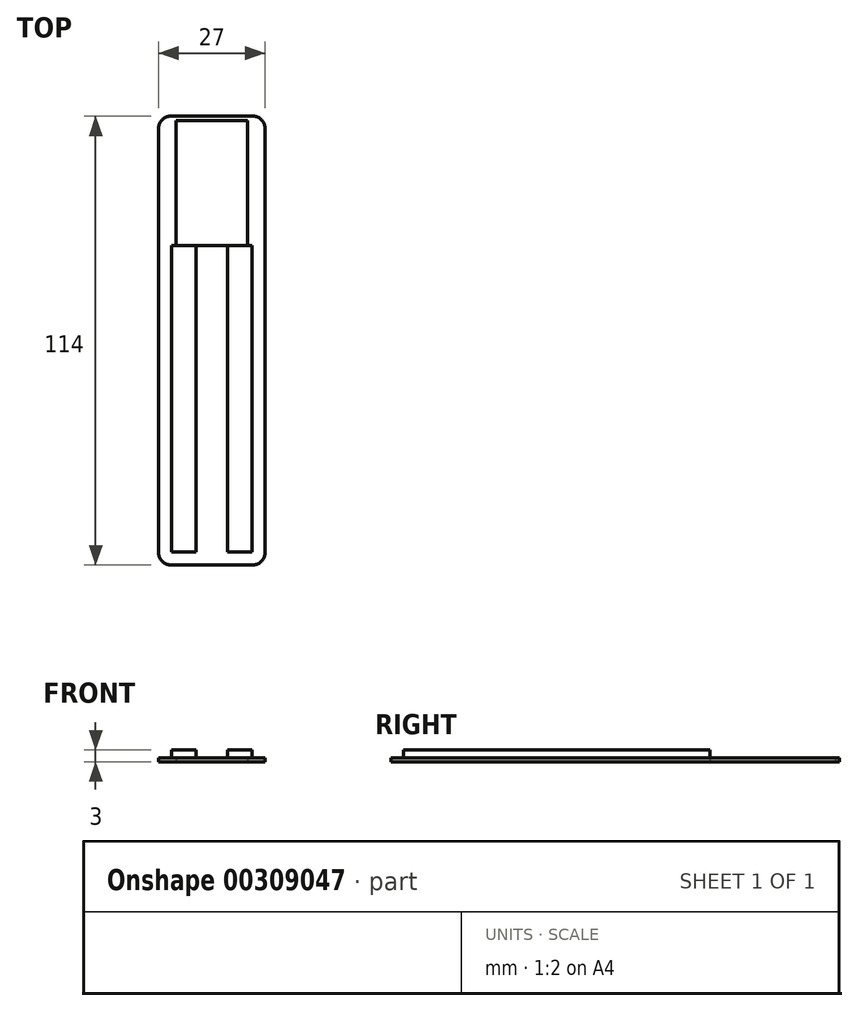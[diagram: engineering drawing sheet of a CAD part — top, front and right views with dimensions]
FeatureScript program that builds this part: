
annotation { "Feature Type Name" : "Feature", "Feature Type Description" : "" }
export const myFeature = defineFeature(function(context is Context, id is Id, definition is map)
    precondition{}
    {
        {
            var Q0;
            Q0=qCreatedBy(makeId("Top.planeOp"),FACE);
            var sketch = newSketch(context, id + "F0", { "sketchPlane" : qUnion([Q0])});
            skLineSegment(sketch, "E0.bottom", {"start": v(-13.5, 57) * mm, "end": v(13.5, 57) * mm});
            skLineSegment(sketch, "E0.top", {"start": v(-13.5, -57) * mm, "end": v(13.5, -57) * mm});
            skLineSegment(sketch, "E0.left", {"start": v(-13.5, 57) * mm, "end": v(-13.5, -57) * mm});
            skLineSegment(sketch, "E0.right", {"start": v(13.5, 57) * mm, "end": v(13.5, -57) * mm});
            skPoint(sketch, "E0.middle", {"position": v(0, 0) * mm});
            skLineSegment(sketch, "E1.bottom", {"start": v(10.27, 24.1) * mm, "end": v(-10.28, 24.1) * mm});
            skLineSegment(sketch, "E1.top", {"start": v(10.28, -53.75) * mm, "end": v(-10.27, -53.75) * mm});
            skLineSegment(sketch, "E1.left", {"start": v(10.27, 24.1) * mm, "end": v(10.28, -53.75) * mm});
            skLineSegment(sketch, "E1.right", {"start": v(-10.28, 24.1) * mm, "end": v(-10.27, -53.75) * mm});
            skPoint(sketch, "E1.middle", {"position": v(0, -14.83) * mm});
            skLineSegment(sketch, "E2.bottom", {"start": v(9.05, 24.1) * mm, "end": v(-9.05, 24.1) * mm});
            skLineSegment(sketch, "E2.top", {"start": v(9.05, 55.9) * mm, "end": v(-9.05, 55.9) * mm});
            skLineSegment(sketch, "E2.left", {"start": v(9.05, 24.1) * mm, "end": v(9.05, 55.9) * mm});
            skLineSegment(sketch, "E2.right", {"start": v(-9.05, 24.1) * mm, "end": v(-9.05, 55.9) * mm});
            skPoint(sketch, "E2.middle", {"position": v(0, 40) * mm});
            skSolve(sketch);
        }
        {
            var Q0;
            Q0=makeQuery(id+"F0.imprint","IMPRINT",FACE,{"disambiguationData":[TD([[makeQuery(id+"F0.imprint","IMPRINT",EDGE,{"derivedFrom":sQuery(id+"F0.wireOp",EDGE,"E0.bottom")}),-1.0]])]});
            extrude(context, id + "F1", {"entities" : qUnion([Q0]), "depth" : 1 * mm});
        }
        {
            var Q0;
            Q0=makeQuery(id+"F0.imprint","IMPRINT",FACE,{"disambiguationData":[TD([[makeQuery(id+"F0.imprint","IMPRINT",EDGE,{"derivedFrom":sQuery(id+"F0.wireOp",EDGE,"E1.top")}),-1.0]])]});
            var Q1;
            Q1=makeQuery(id+"F0.imprint","IMPRINT",FACE,{"disambiguationData":[TD([[makeQuery(id+"F0.imprint","IMPRINT",EDGE,{"derivedFrom":sQuery(id+"F0.wireOp",EDGE,"E2.bottom")}),-1.0]])]});
            extrude(context, id + "F2", {"entities" : qUnion([Q0, Q1]), "operationType" : NewBodyOperationType.ADD, "depth" : 3 * mm});
        }
        {
            var Q0;
            Q0=makeQuery(id+"F1.opExtrude","SWEPT_EDGE",EDGE,{"disambiguationData":[OSD([sQuery(id+"F0.wireOp",EDGE,"E0.top"),sQuery(id+"F0.wireOp",EDGE,"E0.right")])]});
            var Q1;
            Q1=makeQuery(id+"F1.opExtrude","SWEPT_EDGE",EDGE,{"disambiguationData":[OSD([sQuery(id+"F0.wireOp",EDGE,"E0.top"),sQuery(id+"F0.wireOp",EDGE,"E0.left")])]});
            var Q2;
            Q2=makeQuery(id+"F1.opExtrude","SWEPT_EDGE",EDGE,{"disambiguationData":[OSD([sQuery(id+"F0.wireOp",EDGE,"E0.bottom"),sQuery(id+"F0.wireOp",EDGE,"E0.right")])]});
            var Q3;
            Q3=makeQuery(id+"F1.opExtrude","SWEPT_EDGE",EDGE,{"disambiguationData":[OSD([sQuery(id+"F0.wireOp",EDGE,"E0.bottom"),sQuery(id+"F0.wireOp",EDGE,"E0.left")])]});
            fillet(context, id + "F3", {"entities" : qUnion([Q0, Q1, Q2, Q3]), "radius" : 3 * mm, "tangentPropagation" : true, "allowEdgeOverflow" : false});
        }
        {
            var Q0;
            Q0=makeQuery(id+"F2.opExtrude","CAP_FACE",FACE,{"disambiguationData":[OSD([sQuery(id+"F0.wireOp",EDGE,"E1.bottom"),sQuery(id+"F0.wireOp",EDGE,"E1.top"),sQuery(id+"F0.wireOp",EDGE,"E1.left"),sQuery(id+"F0.wireOp",EDGE,"E1.right"),sQuery(id+"F0.wireOp",EDGE,"E2.top"),sQuery(id+"F0.wireOp",EDGE,"E2.left"),sQuery(id+"F0.wireOp",EDGE,"E2.right")])],"isStart":false});
            var sketch = newSketch(context, id + "F4", { "sketchPlane" : qUnion([Q0])});
            skLineSegment(sketch, "E3.bottom", {"start": v(4, -53.75) * mm, "end": v(-4, -53.75) * mm});
            skLineSegment(sketch, "E3.top", {"start": v(4, 55.9) * mm, "end": v(-4, 55.9) * mm});
            skLineSegment(sketch, "E3.left", {"start": v(4, -53.75) * mm, "end": v(4, 55.9) * mm});
            skLineSegment(sketch, "E3.right", {"start": v(-4, -53.75) * mm, "end": v(-4, 55.9) * mm});
            skPoint(sketch, "E3.middle", {"position": v(0, 1.07) * mm});
            skLineSegment(sketch, "E4", {"start": v(-4, 55) * mm, "end": v(4, 55) * mm});
            skSolve(sketch);
        }
        {
            var Q0;
            Q0=makeQuery(id+"F4.imprint","IMPRINT",FACE,{"disambiguationData":[TD([[makeQuery(id+"F4.imprint","IMPRINT",EDGE,{"derivedFrom":sQuery(id+"F4.wireOp",EDGE,"E3.bottom")}),-1.0]])]});
            extrude(context, id + "F5", {"entities" : qUnion([Q0]), "operationType" : NewBodyOperationType.REMOVE, "oppositeDirection" : true, "depth" : 2 * mm});
        }
    });
